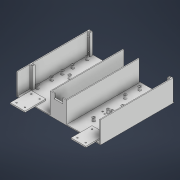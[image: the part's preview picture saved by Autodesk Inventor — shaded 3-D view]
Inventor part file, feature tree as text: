
AUTODESK INVENTOR PART (.ipt)
format: ipt  version: 2021 (Build 250183000, 183)  size: 454,656 bytes
history: native  units: mm
features: extrude x10, sketch x9, projected_geometry x5, fillet x1
ambient origin geometry x8: Origin, YZ Plane, XZ Plane, XY Plane, X Axis, Y Axis, Z Axis, Center Point
bodies: Volumenkörper1 (feature_tree)
feature tree (25):
  extrude  "Extrusion1"  Depth=175.0mm
  extrude  "Extrusion2"  Depth=35.0mm
  extrude  "Extrusion3"  Depth=10.0mm
  extrude  "Extrusion7"  Depth=3.0mm
  extrude  "Extrusion8"  Depth=3.2mm
  extrude  "Extrusion9"  Depth=7.5mm
  extrude  "Extrusion10"  Depth=7.5mm
  extrude  "Extrusion11"  Depth=7.5mm
  fillet  "Rundung1"  Radius=7.5mm
  extrude  "Extrusion12"  Depth=7.5mm
  extrude  "Extrusion13"  Depth=2.0mm TaperAngle=0.0deg
  sketch  "Skizze1"  dims[d0=200.0mm d1=175.0mm]
  sketch  "Skizze2"  dims[d2=2.0mm d3=0.0mm d4=35.0mm]
  sketch  "Skizze3"  dims[d5=50.0mm d6=10.0mm]
  sketch  "Skizze7"  dims[d7=3.0mm d8=0.0mm d9=3.2mm]
  sketch  "Skizze8"  dims[d10=3.2mm d11=3.2mm]
  sketch  "Skizze9"  dims[d12=3.2mm d13=7.5mm]
  sketch  "Skizze10"  dims[d14=7.5mm d15=7.5mm]
  sketch  "Skizze11"  dims[d16=7.5mm d17=7.5mm d18=7.5mm]
  sketch  "Skizze12"  dims[d19=7.5mm d20=7.5mm d21=2.0mm d22=0.0mm d38=2.0mm d39=2.0mm d41=2.0mm d42=6.0mm d43=6.0mm d44=6.0mm d45=6.0mm d66=6.0mm d68=6.0mm d80=50.0mm d81=0.0mm d82=4.0mm d83=4.0mm d84=10.0mm d85=4.0mm d86=4.0mm d87=10.0mm d88=4.0mm d89=4.0mm d90=10.0mm d91=4.0mm d92=10.0mm d93=4.0mm d94=40.0mm d95=0.0mm d96=4.0mm d97=3.0mm d98=3.0mm d99=4.0mm d100=3.0mm d101=3.0mm d102=4.0mm d103=3.0mm d104=3.0mm d105=4.0mm d106=3.0mm d107=3.0mm d108=5.0mm d109=0.0mm d110=3.2mm d111=18.0mm d112=10.0mm d113=10.0mm d114=0.0mm d115=3.2mm d116=3.2mm d117=66.891mm d118=69.627mm d119=42.961mm d120=35.444mm d121=6.0mm d122=30.0mm d123=6.0mm d124=30.0mm d125=90.0deg d127=8.0mm d128=8.0mm d129=98.0mm d130=114.0mm d132=150.0mm d134=150.0mm d149=150.0mm d151=8.0mm d152=98.0mm d153=114.0mm d154=98.0mm d155=150.0mm d157=2.0mm d158=100.0mm d172=2.0mm d173=2.0mm d174=17.5mm d175=17.5mm d176=2.0mm d177=2.0mm d178=20.0mm d179=10.0mm d180=7.5mm d181=10.0mm d182=0.0mm d183=2.0mm d184=7.0mm d185=7.0mm d186=7.0mm d187=7.0mm d188=8.0mm d189=15.0mm d190=15.0mm d191=46.0mm d192=8.0mm d193=46.0mm d194=34.0mm d195=34.0mm d196=7.0mm d197=7.0mm d198=7.0mm d199=7.0mm d200=8.0mm d201=8.0mm d202=50.0mm d203=34.5mm d204=55.0mm d205=50.0mm d206=55.0mm d207=34.5mm d208=7.0mm d209=0.0mm d210=4.0mm d211=0.0mm d212=0.0mm d213=7.0mm d216=4.0mm d217=1.5mm d218=4.0mm d219=0.0mm d220=0.0mm d221=1.5mm d225=7.0mm d226=4.0mm d227=4.0mm d228=4.0mm d229=4.0mm d230=4.0mm d231=4.0mm d232=4.0mm d233=4.0mm d234=4.0mm d235=4.0mm d236=4.0mm d237=4.0mm d238=4.0mm d239=8.0mm d240=0.0mm d241=7.0mm d242=7.0mm d243=7.0mm d244=25.0mm d245=8.0mm d246=25.0mm d247=25.0mm d248=18.0mm d249=18.0mm d250=4.0mm d251=4.0mm d252=4.0mm d253=4.0mm d254=4.0mm d255=4.0mm]
  projected_geometry  "Projizierte Kontur1"
  projected_geometry  "Projizierte Kontur2"
  projected_geometry  "Projizierte Kontur3"
  projected_geometry  "Projizierte Kontur4"
  projected_geometry  "Projizierte Kontur5"
